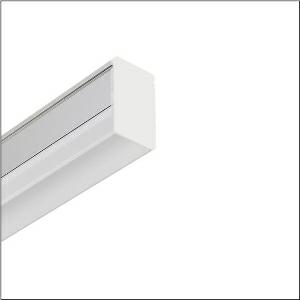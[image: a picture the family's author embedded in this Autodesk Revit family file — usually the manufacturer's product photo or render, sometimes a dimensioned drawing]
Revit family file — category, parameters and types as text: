
# Revit family: siluette_41-f_51lp327dm10af
name_source: partatom
category: Lighting Fixtures
units: mm (PartAtom-declared; Revit-internal decimal feet)

## family parameters
Cut with Voids When Loaded = No
Host = Face
Light Source = No
Part Type = Normal
Room Calculation Point = No
Round Connector Dimension = Use Diameter
Shared = No

## types (1)
- --- (1 x LED, 1000 lm, 8.3 W, 5000K)
    Apparent Load = 8 VA
    CIE Flux Codes = 39 68 88 89 100
    Color Rendering = 80
    Color Temperature = 5000K
    Default Elevation = 1800 mm
    Description = Siluette 41-F, batten luminaire, primary optical cover: cover, of PC, frosted, light emission: direct distribution, primary light characteristic: symmetric, installation type: surface-mounted, LED, rated luminous flux: 1.000lm, luminous efficacy: 120lm/W, light colour: 830/840/850, colour temperature: 3000/4000/5000K, control gear: ON/OFF, with terminal, 2-pole, mains connection: 220..240V, AC, 50/60Hz, rated input power: 8.3W, housing, of aluminium, silver, length: 580mm, width: 25mm, height: 44mm, end cap, of PC, white, protection rating (complete): IP20, insulation class (complete): insulation class II (safety insulation), certification: CE, permissible operating ambient temperature: -20..+40°C, packaging unit: 1 piece
    Height = 44 mm
    Lamp = 1 x LED
    Lamp Light Flux = 1000 lm
    Lamp Power = 8.3 W
    Lamp count = 1
    Length = 580 mm
    Luminous efficacy = 120 lm/W
    Manufacturer = Siteco
    ModVariant = No
    Model = 51LP327DM10AF
    Mounting Place = Ceiling
    Mounting Type = Surface mounted
    Number of Poles = 1
    OnlyDefault = Yes
    Power Factor = 1
    Product Name = Siluette 41-F
    Product group = batten luminaire
    ProductGroupID = 303
    Protection Class = Protection class II
    Protection Degree = IP 20
    RLX_Detail_Level = 1
    RLX_Emergency_Light_Flux = 0 lm
    RLX_Emergency_Type = 0
    RLX_Emergency_Type_DB = No
    RlxData = <blob elided: 27925 chars, md5=fc4d8335>
    Socket = socket
    Standby Power = 0 W
    System Light Flux = 1000 lm
    System Power = 8 W
    Type Comments = individual setting: colour temperature 5000K
    Type Image = l_1007255.jpg
    URL = http://relux.com
    VarID = @adj_037619
    Voltage = 0 V
    Weight = 0.00 kg
    Width = 25 mm  [stored 0.082021 ft]

note: [stored X ft] marks values corroborated as IEEE doubles in the binary element streams (Revit-internal decimal feet)

## geometry (parser evidence)
native form markers: Blend x4, Sweep x12
no freeform markers — native parametric forms only
